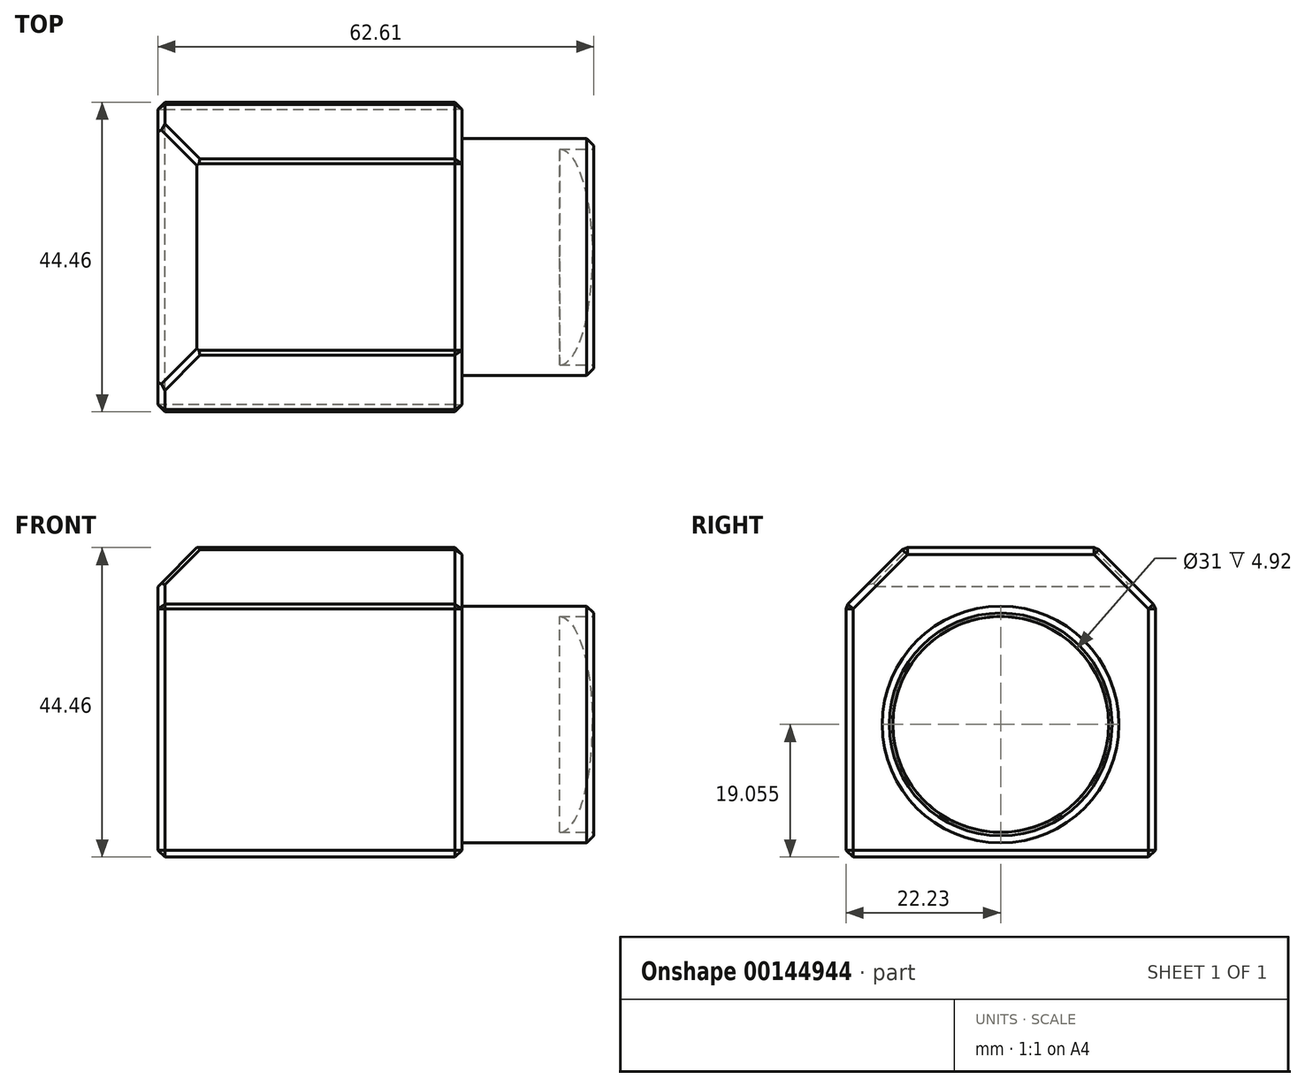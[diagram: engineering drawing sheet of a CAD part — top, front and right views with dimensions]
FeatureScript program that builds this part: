
annotation { "Feature Type Name" : "Feature", "Feature Type Description" : "" }
export const myFeature = defineFeature(function(context is Context, id is Id, definition is map)
    precondition{}
    {
        {
            var Q0;
            Q0=qCreatedBy(makeId("Right.planeOp"),FACE);
            var sketch = newSketch(context, id + "F0", { "sketchPlane" : qUnion([Q0])});
            skLineSegment(sketch, "E0.bottom", {"start": v(22.22, -22.22) * mm, "end": v(-22.23, -22.23) * mm});
            skLineSegment(sketch, "E0.left", {"start": v(22.22, -22.23) * mm, "end": v(22.23, 13.82) * mm});
            skLineSegment(sketch, "E0.right", {"start": v(-22.23, -22.23) * mm, "end": v(-22.23, 13.83) * mm});
            skPoint(sketch, "E0.middle", {"position": v(0, 0) * mm});
            skCircle(sketch, "E1", {"center": v(0, -3.17) * mm, "radius": 17 * mm});
            skLineSegment(sketch, "E2", {"start": v(-22.23, 13.83) * mm, "end": v(-13.83, 22.23) * mm});
            skLineSegment(sketch, "E3", {"start": v(-22.23, 13.83) * mm, "end": v(22.23, 13.83) * mm, "construction": true});
            skLineSegment(sketch, "E4.MirrorCS", {"start": v(22.23, 13.83) * mm, "end": v(13.83, 22.23) * mm});
            skPoint(sketch, "E5.orphan", {"position": v(-22.23, 22.22) * mm});
            skPoint(sketch, "E6.orphan", {"position": v(22.23, 22.23) * mm});
            skLineSegment(sketch, "E7", {"start": v(-13.83, 22.23) * mm, "end": v(13.83, 22.23) * mm});
            skSolve(sketch);
        }
        {
            var Q0;
            Q0=makeQuery(id+"F0.imprint","IMPRINT",FACE,{"disambiguationData":[TD([[makeQuery(id+"F0.imprint","IMPRINT",EDGE,{"derivedFrom":sQuery(id+"F0.wireOp",EDGE,"E1")}),1.0]])]});
            extrude(context, id + "F1", {"entities" : qUnion([Q0]), "depth" : 18.92 * mm, "offsetDistance" : 25 * mm});
        }
        {
            var Q0;
            Q0 = qSketchRegion(id + "F0", true);
            var Q1;
            Q1=makeQuery(id+"F1.opExtrude","CAP_FACE",FACE,{"disambiguationData":[OSD([sQuery(id+"F0.wireOp",EDGE,"E1")])],"isStart":true});
            extrude(context, id + "F2", {"entities" : qUnion([Q0, Q1]), "operationType" : NewBodyOperationType.ADD, "oppositeDirection" : true, "depth" : 43.69 * mm, "offsetDistance" : 25 * mm});
        }
        {
            var Q0;
            Q0=makeQuery(id+"F1.opExtrude","CAP_EDGE",EDGE,{"disambiguationData":[OSD([sQuery(id+"F0.wireOp",EDGE,"E1")])],"isStart":false});
            var Q1;
            Q1=makeQuery(id+"F2.opExtrude","CAP_EDGE",EDGE,{"disambiguationData":[OSD([sQuery(id+"F0.wireOp",EDGE,"E0.right")])],"isStart":true});
            var Q2;
            Q2=makeQuery(id+"F2.opExtrude","CAP_EDGE",EDGE,{"disambiguationData":[OSD([sQuery(id+"F0.wireOp",EDGE,"E2")])],"isStart":true});
            var Q3;
            Q3=makeQuery(id+"F2.opExtrude","CAP_EDGE",EDGE,{"disambiguationData":[OSD([sQuery(id+"F0.wireOp",EDGE,"E7")])],"isStart":true});
            var Q4;
            Q4=makeQuery(id+"F2.opExtrude","CAP_EDGE",EDGE,{"disambiguationData":[OSD([sQuery(id+"F0.wireOp",EDGE,"E4.MirrorCS")])],"isStart":true});
            var Q5;
            Q5=makeQuery(id+"F2.opExtrude","CAP_EDGE",EDGE,{"disambiguationData":[OSD([sQuery(id+"F0.wireOp",EDGE,"E0.left")])],"isStart":true});
            var Q6;
            Q6=makeQuery(id+"F2.opExtrude","CAP_EDGE",EDGE,{"disambiguationData":[OSD([sQuery(id+"F0.wireOp",EDGE,"E0.bottom")])],"isStart":true});
            var Q7;
            {var subQ0=sQuery(id+"F0.wireOp",EDGE,"E1");Q7=makeQuery(id+"F2.boolean.opBoolean","MERGE",FACE,{"derivedFrom":[makeQuery(id+"F2.opExtrude","CAP_FACE",FACE,{"disambiguationData":[OSD([sQuery(id+"F0.wireOp",EDGE,"E0.bottom"),sQuery(id+"F0.wireOp",EDGE,"E0.left"),sQuery(id+"F0.wireOp",EDGE,"E0.right"),subQ0,sQuery(id+"F0.wireOp",EDGE,"E2"),sQuery(id+"F0.wireOp",EDGE,"E4.MirrorCS"),sQuery(id+"F0.wireOp",EDGE,"E7")])],"isStart":false}),makeQuery(id+"F2.opExtrude","CAP_FACE",FACE,{"disambiguationData":[OSD([subQ0])],"isStart":false})]});}
            var Q8;
            Q8=makeQuery(id+"F2.opExtrude","SWEPT_EDGE",EDGE,{"disambiguationData":[OSD([sQuery(id+"F0.wireOp",EDGE,"E0.left"),sQuery(id+"F0.wireOp",EDGE,"E4.MirrorCS")])]});
            var Q9;
            Q9=makeQuery(id+"F2.opExtrude","SWEPT_EDGE",EDGE,{"disambiguationData":[OSD([sQuery(id+"F0.wireOp",EDGE,"E4.MirrorCS"),sQuery(id+"F0.wireOp",EDGE,"E7")])]});
            var Q10;
            Q10=makeQuery(id+"F2.opExtrude","SWEPT_EDGE",EDGE,{"disambiguationData":[OSD([sQuery(id+"F0.wireOp",EDGE,"E0.bottom"),sQuery(id+"F0.wireOp",EDGE,"E0.left")])]});
            var Q11;
            Q11=makeQuery(id+"F2.opExtrude","SWEPT_EDGE",EDGE,{"disambiguationData":[OSD([sQuery(id+"F0.wireOp",EDGE,"E0.bottom"),sQuery(id+"F0.wireOp",EDGE,"E0.right")])]});
            var Q12;
            Q12=makeQuery(id+"F2.opExtrude","SWEPT_EDGE",EDGE,{"disambiguationData":[OSD([sQuery(id+"F0.wireOp",EDGE,"E0.right"),sQuery(id+"F0.wireOp",EDGE,"E2")])]});
            var Q13;
            Q13=makeQuery(id+"F2.opExtrude","SWEPT_EDGE",EDGE,{"disambiguationData":[OSD([sQuery(id+"F0.wireOp",EDGE,"E2"),sQuery(id+"F0.wireOp",EDGE,"E7")])]});
            chamfer(context, id + "F3", {"entities" : qUnion([Q0, Q1, Q2, Q3, Q4, Q5, Q6, Q7, Q8, Q9, Q10, Q11, Q12, Q13]), "width" : 1 * mm, "tangentPropagation" : true});
        }
        {
            var Q0;
            Q0=qCreatedBy(makeId("Front.planeOp"),FACE);
            var sketch = newSketch(context, id + "F4", { "sketchPlane" : qUnion([Q0])});
            skLineSegment(sketch, "E8", {"start": v(0, 13.83) * mm, "end": v(17.97, 13.83) * mm, "construction": true});
            skLineSegment(sketch, "E9", {"start": v(17.97, -20.17) * mm, "end": v(0, -20.17) * mm, "construction": true});
            skLineSegment(sketch, "E10", {"start": v(8.99, 13.83) * mm, "end": v(8.99, -20.17) * mm, "construction": true});
            skLineSegment(sketch, "E11", {"start": v(8.99, -3.17) * mm, "end": v(30.87, -3.17) * mm, "construction": true});
            skEllipticalArc(sketch, "E12", {});
            skLineSegment(sketch, "E13", {"start": v(8.99, -3.17) * mm, "end": v(30.87, -3.17) * mm});
            skPoint(sketch, "E14", {"position": v(14, -18.67) * mm});
            skPoint(sketch, "E15", {"position": v(14, -20.17) * mm});
            skLineSegment(sketch, "E16", {"start": v(14, -18.67) * mm, "end": v(19.42, -18.67) * mm});
            skLineSegment(sketch, "E17", {"start": v(19.42, -18.67) * mm, "end": v(19.42, -3.17) * mm});
            const initialGuessF4  = {"E12": [0.014, -0.003175, 0, -1, 0.0155, 0.004733567915816093, 0, 1.5707963267948966]};
            skSetInitialGuess(sketch, initialGuessF4);
            skSolve(sketch);
        }
        {
            var Q0;
            Q0 = qSketchRegion(id + "F4", true);
            var Q1;
            Q1=sQuery(id+"F4.wireOp",EDGE,"E13");
            revolve(context, id + "F5", {"operationType" : NewBodyOperationType.REMOVE, "surfaceOperationType" : NewSurfaceOperationType.NEW, "entities" : qUnion([Q0]), "axis" : qUnion([Q1]), "revolveType" : RevolveType.FULL, "oppositeDirection" : true});
        }
        {
            var Q0;
            Q0=makeQuery(id+"F2.opExtrude","SWEPT_FACE",FACE,{"disambiguationData":[OSD([sQuery(id+"F0.wireOp",EDGE,"E0.right")])]});
            var sketch = newSketch(context, id + "F6", { "sketchPlane" : qUnion([Q0])});
            skLineSegment(sketch, "E18", {"start": v(-43.69, 22.23) * mm, "end": v(-43.69, 16.61) * mm});
            skLineSegment(sketch, "E19", {"start": v(-43.69, 16.61) * mm, "end": v(-38.08, 22.23) * mm});
            skLineSegment(sketch, "E20", {"start": v(-38.08, 22.23) * mm, "end": v(-43.69, 22.23) * mm});
            skLineSegment(sketch, "E21.0", {"start": v(-42.69, 22.22) * mm, "end": v(-1, 22.22) * mm, "construction": true});
            skLineSegment(sketch, "E22.0", {"start": v(-43.69, 13.41) * mm, "end": v(-43.69, 21.23) * mm, "construction": true});
            skSolve(sketch);
        }
        {
            var Q0;
            Q0 = qSketchRegion(id + "F6", true);
            var Q1;
            Q1=makeQuery(id+"F2.opExtrude","SWEPT_FACE",FACE,{"disambiguationData":[OSD([sQuery(id+"F0.wireOp",EDGE,"E0.left")])]});
            extrude(context, id + "F7", {"entities" : qUnion([Q0]), "operationType" : NewBodyOperationType.REMOVE, "endBound" : BoundingType.UP_TO_SURFACE, "oppositeDirection" : true, "depth" : 25 * mm, "endBoundEntityFace" : qUnion([Q1]), "offsetDistance" : 25 * mm});
        }
        {
            var Q0;
            Q0=makeQuery(id+"F7.boolean.opBoolean","COPY",EDGE,{"derivedFrom":makeQuery(id+"F7.opExtrude","SWEPT_EDGE",EDGE,{"disambiguationData":[OSD([sQuery(id+"F6.wireOp",EDGE,"E19"),sQuery(id+"F6.wireOp",EDGE,"E20")])]})});
            var Q1;
            Q1=makeQuery(id+"F7.boolean.opBoolean","INTERSECT",EDGE,{"derivedFrom":[makeQuery(id+"F2.opExtrude","SWEPT_FACE",FACE,{"disambiguationData":[OSD([sQuery(id+"F0.wireOp",EDGE,"E2")])]}),makeQuery(id+"F7.opExtrude","SWEPT_FACE",FACE,{"disambiguationData":[OSD([sQuery(id+"F6.wireOp",EDGE,"E19")])]})]});
            var Q2;
            Q2=makeQuery(id+"F7.boolean.opBoolean","INTERSECT",EDGE,{"derivedFrom":[makeQuery(id+"F2.opExtrude","SWEPT_FACE",FACE,{"disambiguationData":[OSD([sQuery(id+"F0.wireOp",EDGE,"E4.MirrorCS")])]}),makeQuery(id+"F7.opExtrude","SWEPT_FACE",FACE,{"disambiguationData":[OSD([sQuery(id+"F6.wireOp",EDGE,"E19")])]})]});
            var Q3;
            Q3=makeQuery(id+"F7.boolean.opBoolean","COPY",EDGE,{"derivedFrom":makeQuery(id+"F7.opExtrude","SWEPT_EDGE",EDGE,{"disambiguationData":[OSD([sQuery(id+"F6.wireOp",EDGE,"E18"),sQuery(id+"F6.wireOp",EDGE,"E19")])]})});
            chamfer(context, id + "F8", {"entities" : qUnion([Q0, Q1, Q2, Q3]), "width" : 1 * mm, "tangentPropagation" : true});
        }
    });
